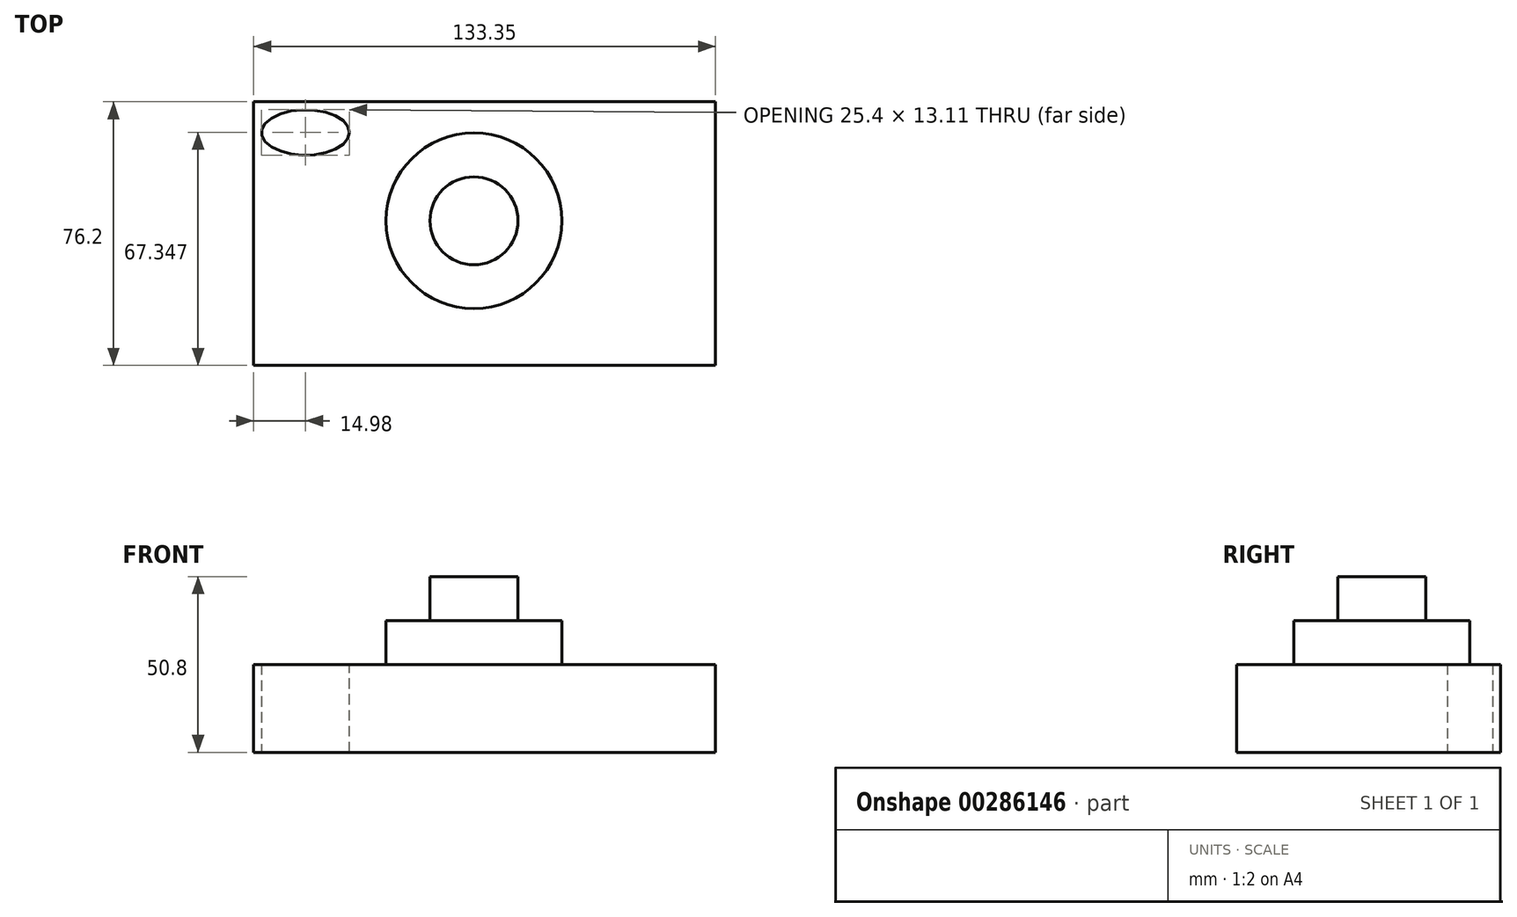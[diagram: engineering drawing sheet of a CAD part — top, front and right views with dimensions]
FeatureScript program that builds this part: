
annotation { "Feature Type Name" : "Feature", "Feature Type Description" : "" }
export const myFeature = defineFeature(function(context is Context, id is Id, definition is map)
    precondition{}
    {
        {
            var Q0;
            Q0=qCreatedBy(makeId("Top.planeOp"),FACE);
            var sketch = newSketch(context, id + "F0", { "sketchPlane" : qUnion([Q0])});
            skLineSegment(sketch, "E0.bottom", {"start": v(0, 0) * mm, "end": v(-133.35, 0) * mm});
            skLineSegment(sketch, "E0.top", {"start": v(0, 76.2) * mm, "end": v(-133.35, 76.2) * mm});
            skLineSegment(sketch, "E0.left", {"start": v(0, 0) * mm, "end": v(0, 76.2) * mm});
            skLineSegment(sketch, "E0.right", {"start": v(-133.35, 0) * mm, "end": v(-133.35, 76.2) * mm});
            skSolve(sketch);
        }
        {
            var Q0;
            Q0=makeQuery(id+"F0.imprint","IMPRINT",FACE,{"disambiguationData":[TD([[makeQuery(id+"F0.imprint","IMPRINT",EDGE,{"derivedFrom":sQuery(id+"F0.wireOp",EDGE,"E0.bottom")}),-1.0]])]});
            extrude(context, id + "F1", {"entities" : qUnion([Q0]), "depth" : 25.4 * mm});
        }
        {
            var Q0;
            Q0=makeQuery(id+"F1.opExtrude","CAP_FACE",FACE,{"disambiguationData":[OSD([sQuery(id+"F0.wireOp",EDGE,"E0.bottom"),sQuery(id+"F0.wireOp",EDGE,"E0.top"),sQuery(id+"F0.wireOp",EDGE,"E0.left"),sQuery(id+"F0.wireOp",EDGE,"E0.right")])],"isStart":false});
            var sketch = newSketch(context, id + "F2", { "sketchPlane" : qUnion([Q0])});
            skCircle(sketch, "E1", {"center": v(-69.74, 41.82) * mm, "radius": 25.4 * mm});
            skSolve(sketch);
        }
        {
            var Q0;
            Q0 = qSketchRegion(id + "F2", true);
            extrude(context, id + "F3", {"entities" : qUnion([Q0]), "operationType" : NewBodyOperationType.ADD, "depth" : 12.7 * mm});
        }
        {
            var Q0;
            Q0=makeQuery(id+"F3.opExtrude","CAP_FACE",FACE,{"disambiguationData":[OSD([sQuery(id+"F2.wireOp",EDGE,"E1")])],"isStart":false});
            var sketch = newSketch(context, id + "F4", { "sketchPlane" : qUnion([Q0])});
            skCircle(sketch, "E2", {"center": v(-69.74, 41.82) * mm, "radius": 12.7 * mm});
            skSolve(sketch);
        }
        {
            var Q0;
            Q0 = qSketchRegion(id + "F4", true);
            extrude(context, id + "F5", {"entities" : qUnion([Q0]), "operationType" : NewBodyOperationType.ADD, "depth" : 12.7 * mm});
        }
        {
            var Q0;
            Q0=makeQuery(id+"F1.opExtrude","CAP_FACE",FACE,{"disambiguationData":[OSD([sQuery(id+"F0.wireOp",EDGE,"E0.bottom"),sQuery(id+"F0.wireOp",EDGE,"E0.top"),sQuery(id+"F0.wireOp",EDGE,"E0.left"),sQuery(id+"F0.wireOp",EDGE,"E0.right")])],"isStart":false});
            var sketch = newSketch(context, id + "F6", { "sketchPlane" : qUnion([Q0])});
            skEllipse(sketch, "E3", {"center": v(-118.37, 67.35) * mm, "majorRadius": 12.7 * mm, "minorRadius": 6.55 * mm, "majorAxis": v(1, 0)});
            skSolve(sketch);
        }
        {
            var Q0;
            Q0 = qSketchRegion(id + "F6", true);
            extrude(context, id + "F7", {"entities" : qUnion([Q0]), "operationType" : NewBodyOperationType.REMOVE, "endBound" : BoundingType.THROUGH_ALL, "oppositeDirection" : true, "depth" : 25.4 * mm});
        }
    });
